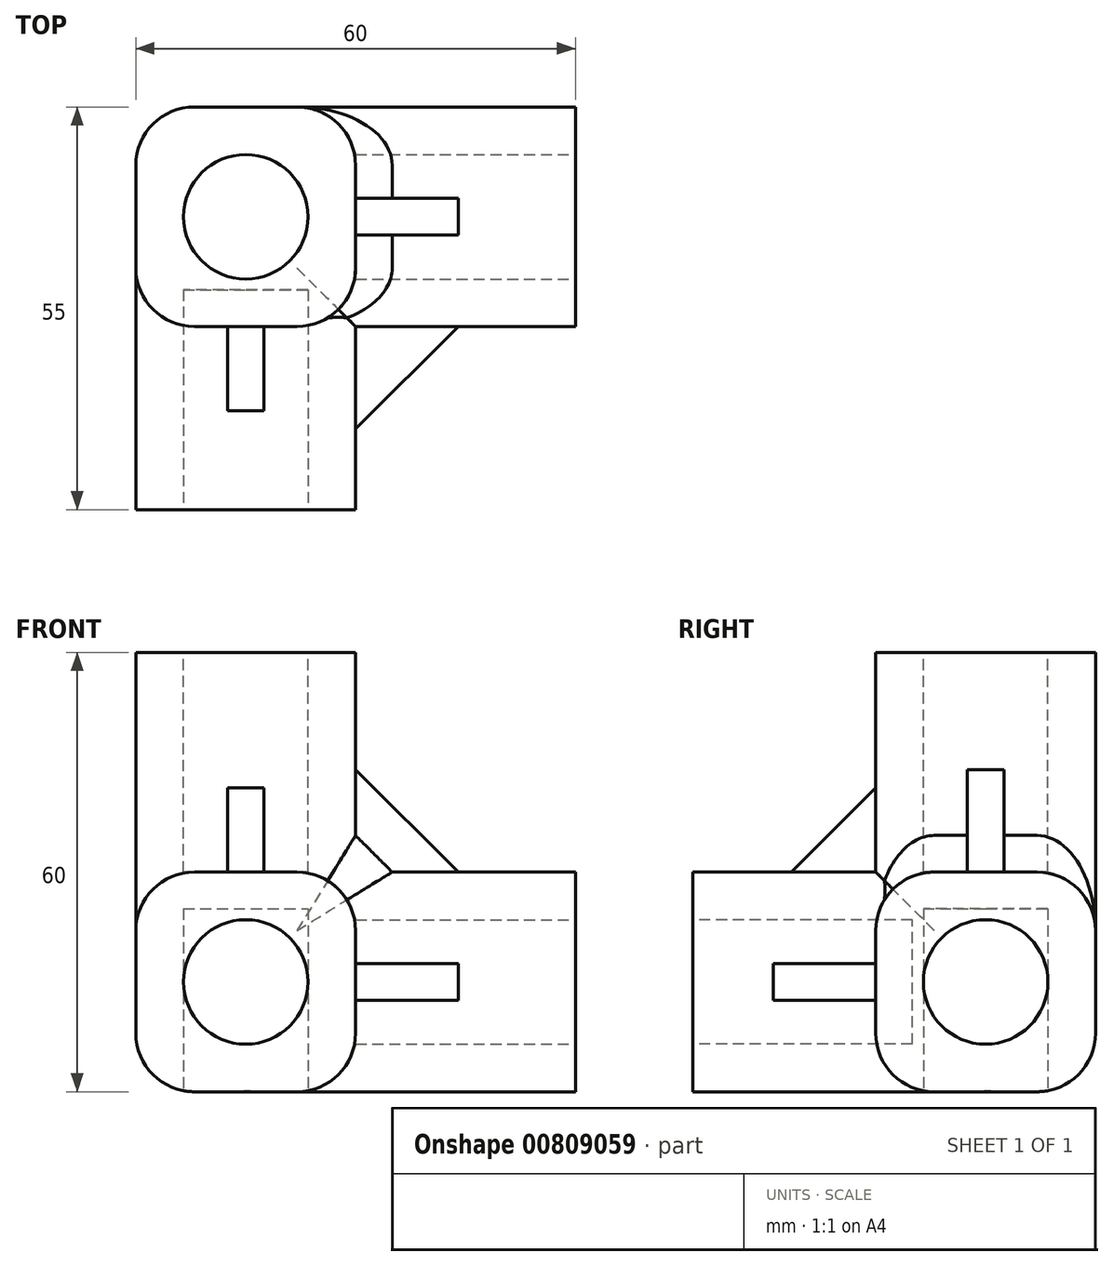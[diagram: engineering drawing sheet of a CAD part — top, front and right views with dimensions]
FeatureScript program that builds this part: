
annotation { "Feature Type Name" : "Feature", "Feature Type Description" : "" }
export const myFeature = defineFeature(function(context is Context, id is Id, definition is map)
    precondition{}
    {
        {
            var Q0;
            Q0=qCreatedBy(makeId("Top.planeOp"),FACE);
            var sketch = newSketch(context, id + "F0", { "sketchPlane" : qUnion([Q0])});
            skLineSegment(sketch, "E0.bottom", {"start": v(-15, 15) * mm, "end": v(15, 15) * mm});
            skLineSegment(sketch, "E0.top", {"start": v(-15, -15) * mm, "end": v(15, -15) * mm});
            skLineSegment(sketch, "E0.left", {"start": v(-15, 15) * mm, "end": v(-15, -15) * mm});
            skLineSegment(sketch, "E0.right", {"start": v(15, 15) * mm, "end": v(15, -15) * mm});
            skSolve(sketch);
        }
        {
            var Q0;
            Q0=qSketchRegion(id+"F0",true);
            extrude(context, id + "F1", {"entities" : qUnion([Q0]), "depth" : 30 * mm, "offsetDistance" : 25 * mm});
        }
        {
            var Q0;
            Q0=makeQuery(id+"F1.opExtrude","SWEPT_FACE",FACE,{"disambiguationData":[OSD([sQuery(id+"F0.wireOp",EDGE,"E0.top")])]});
            var sketch = newSketch(context, id + "F2", { "sketchPlane" : qUnion([Q0])});
            skLineSegment(sketch, "E1.bottom", {"start": v(-15, 0) * mm, "end": v(15, 0) * mm});
            skLineSegment(sketch, "E1.top", {"start": v(-15, 30) * mm, "end": v(15, 30) * mm});
            skLineSegment(sketch, "E1.left", {"start": v(-15, 0) * mm, "end": v(-15, 30) * mm});
            skLineSegment(sketch, "E1.right", {"start": v(15, 0) * mm, "end": v(15, 30) * mm});
            skSolve(sketch);
        }
        {
            var Q0;
            Q0=qSketchRegion(id+"F2",true);
            extrude(context, id + "F3", {"entities" : qUnion([Q0]), "operationType" : NewBodyOperationType.ADD, "depth" : 25 * mm, "offsetDistance" : 25 * mm});
        }
        {
            var Q0;
            Q0=makeQuery(id+"F3.opExtrude","CAP_FACE",FACE,{"disambiguationData":[OSD([sQuery(id+"F2.wireOp",EDGE,"E1.bottom"),sQuery(id+"F2.wireOp",EDGE,"E1.top"),sQuery(id+"F2.wireOp",EDGE,"E1.left"),sQuery(id+"F2.wireOp",EDGE,"E1.right")])],"isStart":false});
            var sketch = newSketch(context, id + "F4", { "sketchPlane" : qUnion([Q0])});
            skLineSegment(sketch, "E2", {"start": v(0, 30) * mm, "end": v(0, 0) * mm, "construction": true});
            skCircle(sketch, "E3", {"center": v(0, 15) * mm, "radius": 8.5 * mm});
            skSolve(sketch);
        }
        {
            var Q0;
            Q0=qSketchRegion(id+"F4",true);
            extrude(context, id + "F5", {"entities" : qUnion([Q0]), "operationType" : NewBodyOperationType.REMOVE, "oppositeDirection" : true, "depth" : 30 * mm, "offsetDistance" : 25 * mm});
        }
        {
            var Q0;
            Q0=makeQuery(id+"F3.boolean.opBoolean","MERGE",FACE,{"derivedFrom":[makeQuery(id+"F1.opExtrude","SWEPT_FACE",FACE,{"disambiguationData":[OSD([sQuery(id+"F0.wireOp",EDGE,"E0.right")])]}),makeQuery(id+"F3.opExtrude","SWEPT_FACE",FACE,{"disambiguationData":[OSD([sQuery(id+"F2.wireOp",EDGE,"E1.right")])]})]});
            var sketch = newSketch(context, id + "F6", { "sketchPlane" : qUnion([Q0])});
            skLineSegment(sketch, "E4.bottom", {"start": v(15, 0) * mm, "end": v(-15, 0) * mm});
            skLineSegment(sketch, "E4.top", {"start": v(15, 30) * mm, "end": v(-15, 30) * mm});
            skLineSegment(sketch, "E4.left", {"start": v(15, 0) * mm, "end": v(15, 30) * mm});
            skLineSegment(sketch, "E4.right", {"start": v(-15, 0) * mm, "end": v(-15, 30) * mm});
            skSolve(sketch);
        }
        {
            var Q0;
            Q0=qSketchRegion(id+"F6",true);
            extrude(context, id + "F7", {"entities" : qUnion([Q0]), "operationType" : NewBodyOperationType.ADD, "depth" : 30 * mm, "offsetDistance" : 25 * mm});
        }
        {
            var Q0;
            Q0=makeQuery(id+"F7.opExtrude","CAP_FACE",FACE,{"disambiguationData":[OSD([sQuery(id+"F6.wireOp",EDGE,"E4.bottom"),sQuery(id+"F6.wireOp",EDGE,"E4.top"),sQuery(id+"F6.wireOp",EDGE,"E4.left"),sQuery(id+"F6.wireOp",EDGE,"E4.right")])],"isStart":false});
            var sketch = newSketch(context, id + "F8", { "sketchPlane" : qUnion([Q0])});
            skCircle(sketch, "E5", {"center": v(0, 15) * mm, "radius": 8.5 * mm});
            skSolve(sketch);
        }
        {
            var Q0;
            Q0=qSketchRegion(id+"F8",true);
            extrude(context, id + "F9", {"entities" : qUnion([Q0]), "operationType" : NewBodyOperationType.REMOVE, "oppositeDirection" : true, "depth" : 30 * mm, "offsetDistance" : 25 * mm});
        }
        {
            var Q0;
            Q0=makeQuery(id+"F7.boolean.opBoolean","MERGE",FACE,{"derivedFrom":[makeQuery(id+"F3.boolean.opBoolean","MERGE",FACE,{"derivedFrom":[makeQuery(id+"F1.opExtrude","CAP_FACE",FACE,{"disambiguationData":[OSD([sQuery(id+"F0.wireOp",EDGE,"E0.bottom"),sQuery(id+"F0.wireOp",EDGE,"E0.top"),sQuery(id+"F0.wireOp",EDGE,"E0.left"),sQuery(id+"F0.wireOp",EDGE,"E0.right")])],"isStart":false}),makeQuery(id+"F3.opExtrude","SWEPT_FACE",FACE,{"disambiguationData":[OSD([sQuery(id+"F2.wireOp",EDGE,"E1.top")])]})]}),makeQuery(id+"F7.opExtrude","SWEPT_FACE",FACE,{"disambiguationData":[OSD([sQuery(id+"F6.wireOp",EDGE,"E4.top")])]})]});
            var sketch = newSketch(context, id + "F10", { "sketchPlane" : qUnion([Q0])});
            skLineSegment(sketch, "E6.bottom", {"start": v(-15, 15) * mm, "end": v(15, 15) * mm});
            skLineSegment(sketch, "E6.top", {"start": v(-15, -15) * mm, "end": v(15, -15) * mm});
            skLineSegment(sketch, "E6.left", {"start": v(-15, 15) * mm, "end": v(-15, -15) * mm});
            skLineSegment(sketch, "E6.right", {"start": v(15, 15) * mm, "end": v(15, -15) * mm});
            skSolve(sketch);
        }
        {
            var Q0;
            Q0=qSketchRegion(id+"F10",true);
            extrude(context, id + "F11", {"entities" : qUnion([Q0]), "operationType" : NewBodyOperationType.ADD, "depth" : 30 * mm, "offsetDistance" : 25 * mm});
        }
        {
            var Q0;
            Q0=makeQuery(id+"F11.opExtrude","CAP_FACE",FACE,{"disambiguationData":[OSD([sQuery(id+"F10.wireOp",EDGE,"E6.bottom"),sQuery(id+"F10.wireOp",EDGE,"E6.top"),sQuery(id+"F10.wireOp",EDGE,"E6.left"),sQuery(id+"F10.wireOp",EDGE,"E6.right")])],"isStart":false});
            var sketch = newSketch(context, id + "F12", { "sketchPlane" : qUnion([Q0])});
            skCircle(sketch, "E7", {"center": v(0, 0) * mm, "radius": 8.5 * mm});
            skSolve(sketch);
        }
        {
            var Q0;
            Q0=qSketchRegion(id+"F12",true);
            extrude(context, id + "F13", {"entities" : qUnion([Q0]), "operationType" : NewBodyOperationType.REMOVE, "oppositeDirection" : true, "depth" : 30 * mm, "offsetDistance" : 25 * mm});
        }
        {
            var Q0;
            Q0=makeQuery(id+"F11.opExtrude","SWEPT_EDGE",EDGE,{"disambiguationData":[OSD([sQuery(id+"F0.wireOp",EDGE,"E0.left"),sQuery(id+"F2.wireOp",EDGE,"E1.top"),sQuery(id+"F2.wireOp",EDGE,"E1.left"),sQuery(id+"F10.wireOp",EDGE,"E6.top"),sQuery(id+"F10.wireOp",EDGE,"E6.left")])]});
            var Q1;
            Q1=makeQuery(id+"F3.boolean.opBoolean","MERGE",EDGE,{"derivedFrom":[makeQuery(id+"F1.opExtrude","CAP_EDGE",EDGE,{"disambiguationData":[OSD([sQuery(id+"F0.wireOp",EDGE,"E0.left")])],"isStart":false}),makeQuery(id+"F3.opExtrude","SWEPT_EDGE",EDGE,{"disambiguationData":[OSD([sQuery(id+"F2.wireOp",EDGE,"E1.top"),sQuery(id+"F2.wireOp",EDGE,"E1.left")])]})]});
            var Q2;
            Q2=makeQuery(id+"F3.boolean.opBoolean","MERGE",EDGE,{"derivedFrom":[makeQuery(id+"F1.opExtrude","CAP_EDGE",EDGE,{"disambiguationData":[OSD([sQuery(id+"F0.wireOp",EDGE,"E0.left")])],"isStart":true}),makeQuery(id+"F3.opExtrude","SWEPT_EDGE",EDGE,{"disambiguationData":[OSD([sQuery(id+"F2.wireOp",EDGE,"E1.bottom"),sQuery(id+"F2.wireOp",EDGE,"E1.left")])]})]});
            var Q3;
            Q3=makeQuery(id+"F11.boolean.opBoolean","MERGE",EDGE,{"derivedFrom":[makeQuery(id+"F1.opExtrude","SWEPT_EDGE",EDGE,{"disambiguationData":[OSD([sQuery(id+"F0.wireOp",EDGE,"E0.bottom"),sQuery(id+"F0.wireOp",EDGE,"E0.left")])]}),makeQuery(id+"F11.opExtrude","SWEPT_EDGE",EDGE,{"disambiguationData":[OSD([sQuery(id+"F10.wireOp",EDGE,"E6.bottom"),sQuery(id+"F10.wireOp",EDGE,"E6.left")])]})]});
            var Q4;
            Q4=makeQuery(id+"F3.boolean.opBoolean","MERGE",EDGE,{"derivedFrom":[makeQuery(id+"F1.opExtrude","CAP_EDGE",EDGE,{"disambiguationData":[OSD([sQuery(id+"F0.wireOp",EDGE,"E0.right")])],"isStart":true}),makeQuery(id+"F3.opExtrude","SWEPT_EDGE",EDGE,{"disambiguationData":[OSD([sQuery(id+"F2.wireOp",EDGE,"E1.bottom"),sQuery(id+"F2.wireOp",EDGE,"E1.right")])]})]});
            var Q5;
            Q5=makeQuery(id+"F3.boolean.opBoolean","MERGE",EDGE,{"derivedFrom":[makeQuery(id+"F1.opExtrude","CAP_EDGE",EDGE,{"disambiguationData":[OSD([sQuery(id+"F0.wireOp",EDGE,"E0.right")])],"isStart":false}),makeQuery(id+"F3.opExtrude","SWEPT_EDGE",EDGE,{"disambiguationData":[OSD([sQuery(id+"F2.wireOp",EDGE,"E1.top"),sQuery(id+"F2.wireOp",EDGE,"E1.right")])]})]});
            fillet(context, id + "F14", {"entities" : qUnion([Q0, Q1, Q2, Q3, Q4, Q5]), "radius" : 8 * mm, "tangentPropagation" : true, "allowEdgeOverflow" : false});
        }
        {
            var Q0;
            Q0=makeQuery(id+"F11.opExtrude","SWEPT_EDGE",EDGE,{"disambiguationData":[OSD([sQuery(id+"F0.wireOp",EDGE,"E0.right"),sQuery(id+"F2.wireOp",EDGE,"E1.top"),sQuery(id+"F2.wireOp",EDGE,"E1.right"),sQuery(id+"F6.wireOp",EDGE,"E4.top"),sQuery(id+"F6.wireOp",EDGE,"E4.right"),sQuery(id+"F10.wireOp",EDGE,"E6.top"),sQuery(id+"F10.wireOp",EDGE,"E6.right")])]});
            var Q1;
            Q1=makeQuery(id+"F7.opExtrude","SWEPT_EDGE",EDGE,{"disambiguationData":[OSD([sQuery(id+"F0.wireOp",EDGE,"E0.right"),sQuery(id+"F2.wireOp",EDGE,"E1.top"),sQuery(id+"F2.wireOp",EDGE,"E1.right"),sQuery(id+"F6.wireOp",EDGE,"E4.top"),sQuery(id+"F6.wireOp",EDGE,"E4.right")])]});
            var Q2;
            Q2=makeQuery(id+"F11.opExtrude","SWEPT_EDGE",EDGE,{"disambiguationData":[OSD([sQuery(id+"F0.wireOp",EDGE,"E0.bottom"),sQuery(id+"F6.wireOp",EDGE,"E4.top"),sQuery(id+"F6.wireOp",EDGE,"E4.left"),sQuery(id+"F10.wireOp",EDGE,"E6.bottom"),sQuery(id+"F10.wireOp",EDGE,"E6.right")])]});
            var Q3;
            Q3=makeQuery(id+"F7.boolean.opBoolean","MERGE",EDGE,{"derivedFrom":[makeQuery(id+"F1.opExtrude","CAP_EDGE",EDGE,{"disambiguationData":[OSD([sQuery(id+"F0.wireOp",EDGE,"E0.bottom")])],"isStart":false}),makeQuery(id+"F7.opExtrude","SWEPT_EDGE",EDGE,{"disambiguationData":[OSD([sQuery(id+"F6.wireOp",EDGE,"E4.top"),sQuery(id+"F6.wireOp",EDGE,"E4.left")])]})]});
            var Q4;
            Q4=makeQuery(id+"F7.opExtrude","SWEPT_EDGE",EDGE,{"disambiguationData":[OSD([sQuery(id+"F0.wireOp",EDGE,"E0.right"),sQuery(id+"F2.wireOp",EDGE,"E1.bottom"),sQuery(id+"F2.wireOp",EDGE,"E1.right"),sQuery(id+"F6.wireOp",EDGE,"E4.bottom"),sQuery(id+"F6.wireOp",EDGE,"E4.right")])]});
            var Q5;
            Q5=makeQuery(id+"F7.boolean.opBoolean","MERGE",EDGE,{"derivedFrom":[makeQuery(id+"F1.opExtrude","CAP_EDGE",EDGE,{"disambiguationData":[OSD([sQuery(id+"F0.wireOp",EDGE,"E0.bottom")])],"isStart":true}),makeQuery(id+"F7.opExtrude","SWEPT_EDGE",EDGE,{"disambiguationData":[OSD([sQuery(id+"F6.wireOp",EDGE,"E4.bottom"),sQuery(id+"F6.wireOp",EDGE,"E4.left")])]})]});
            fillet(context, id + "F15", {"entities" : qUnion([Q0, Q1, Q2, Q3, Q4, Q5]), "radius" : 8 * mm, "tangentPropagation" : true, "allowEdgeOverflow" : false});
        }
        {
            var Q0;
            Q0=makeQuery(id+"F7.opExtrude","CAP_EDGE",EDGE,{"disambiguationData":[OSD([sQuery(id+"F6.wireOp",EDGE,"E4.right")])],"isStart":true});
            var Q1;
            Q1=makeQuery(id+"F11.opExtrude","CAP_EDGE",EDGE,{"disambiguationData":[OSD([sQuery(id+"F10.wireOp",EDGE,"E6.top")])],"isStart":true});
            var Q2;
            Q2=makeQuery(id+"F11.opExtrude","CAP_EDGE",EDGE,{"disambiguationData":[OSD([sQuery(id+"F10.wireOp",EDGE,"E6.right")])],"isStart":true});
            chamfer(context, id + "F16", {"entities" : qUnion([Q0, Q1, Q2]), "width" : 5 * mm, "tangentPropagation" : true});
        }
        {
            var Q0;
            Q0=qCreatedBy(makeId("Right.planeOp"),FACE);
            var sketch = newSketch(context, id + "F17", { "sketchPlane" : qUnion([Q0])});
            skLineSegment(sketch, "E8", {"start": v(-26.5, 30) * mm, "end": v(-12.5, 44) * mm});
            skLineSegment(sketch, "E9", {"start": v(-12.5, 44) * mm, "end": v(-12.5, 30) * mm});
            skLineSegment(sketch, "E10", {"start": v(-12.5, 30) * mm, "end": v(-26.5, 30) * mm});
            skSolve(sketch);
        }
        {
            var Q0;
            Q0=qSketchRegion(id+"F17",true);
            extrude(context, id + "F18", {"entities" : qUnion([Q0]), "operationType" : NewBodyOperationType.ADD, "depth" : 2.5 * mm, "offsetDistance" : 25 * mm});
        }
        {
            var Q0;
            Q0=qSketchRegion(id+"F17",true);
            extrude(context, id + "F19", {"entities" : qUnion([Q0]), "operationType" : NewBodyOperationType.ADD, "oppositeDirection" : true, "depth" : 2.5 * mm, "offsetDistance" : 25 * mm});
        }
        {
            var Q0;
            Q0=qCreatedBy(makeId("Front.planeOp"),FACE);
            var sketch = newSketch(context, id + "F20", { "sketchPlane" : qUnion([Q0])});
            skLineSegment(sketch, "E11", {"start": v(29, 30) * mm, "end": v(15, 44) * mm});
            skLineSegment(sketch, "E12", {"start": v(15, 44) * mm, "end": v(15, 30) * mm});
            skLineSegment(sketch, "E13", {"start": v(15, 30) * mm, "end": v(29, 30) * mm});
            skSolve(sketch);
        }
        {
            var Q0;
            Q0=qSketchRegion(id+"F20",true);
            extrude(context, id + "F21", {"entities" : qUnion([Q0]), "operationType" : NewBodyOperationType.ADD, "depth" : 2.5 * mm, "offsetDistance" : 25 * mm});
        }
        {
            var Q0;
            Q0=qSketchRegion(id+"F20",true);
            extrude(context, id + "F22", {"entities" : qUnion([Q0]), "operationType" : NewBodyOperationType.ADD, "oppositeDirection" : true, "depth" : 2.5 * mm, "offsetDistance" : 25 * mm});
        }
        {
            var Q0;
            Q0=qCreatedBy(makeId("Top.planeOp"),FACE);
            cPlane(context, id + "F23", {"entities" : qUnion([Q0]), "cplaneType" : CPlaneType.OFFSET, "offset" : 15 * mm, "width" : 150 * mm, "height" : 150 * mm});
        }
        {
            var Q0;
            Q0=qCreatedBy(id+"F23.planeOp",FACE);
            var sketch = newSketch(context, id + "F24", { "sketchPlane" : qUnion([Q0])});
            skLineSegment(sketch, "E14", {"start": v(15, -29) * mm, "end": v(29, -15) * mm});
            skLineSegment(sketch, "E15", {"start": v(29, -15) * mm, "end": v(15, -15) * mm});
            skLineSegment(sketch, "E16", {"start": v(15, -15) * mm, "end": v(15, -29) * mm});
            skSolve(sketch);
        }
        {
            var Q0;
            Q0=qSketchRegion(id+"F24",true);
            extrude(context, id + "F25", {"entities" : qUnion([Q0]), "operationType" : NewBodyOperationType.ADD, "depth" : 2.5 * mm, "offsetDistance" : 25 * mm});
        }
        {
            var Q0;
            Q0=qSketchRegion(id+"F24",true);
            extrude(context, id + "F26", {"entities" : qUnion([Q0]), "operationType" : NewBodyOperationType.ADD, "oppositeDirection" : true, "depth" : 2.5 * mm, "offsetDistance" : 25 * mm});
        }
        {
            var Q0;
            Q0=makeQuery(id+"F7.boolean.opBoolean","MERGE",FACE,{"derivedFrom":[makeQuery(id+"F3.boolean.opBoolean","MERGE",FACE,{"derivedFrom":[makeQuery(id+"F1.opExtrude","CAP_FACE",FACE,{"disambiguationData":[OSD([sQuery(id+"F0.wireOp",EDGE,"E0.bottom"),sQuery(id+"F0.wireOp",EDGE,"E0.top"),sQuery(id+"F0.wireOp",EDGE,"E0.left"),sQuery(id+"F0.wireOp",EDGE,"E0.right")])],"isStart":true}),makeQuery(id+"F3.opExtrude","SWEPT_FACE",FACE,{"disambiguationData":[OSD([sQuery(id+"F2.wireOp",EDGE,"E1.bottom")])]})]}),makeQuery(id+"F7.opExtrude","SWEPT_FACE",FACE,{"disambiguationData":[OSD([sQuery(id+"F6.wireOp",EDGE,"E4.bottom")])]})]});
            var sketch = newSketch(context, id + "F27", { "sketchPlane" : qUnion([Q0])});
            skCircle(sketch, "E17", {"center": v(0, 0) * mm, "radius": 8.5 * mm});
            skSolve(sketch);
        }
        {
            var Q0;
            Q0 = qSketchRegion(id + "F27", true);
            extrude(context, id + "F28", {"entities" : qUnion([Q0]), "operationType" : NewBodyOperationType.REMOVE, "oppositeDirection" : true, "depth" : 25 * mm, "offsetDistance" : 25 * mm});
        }
    });
